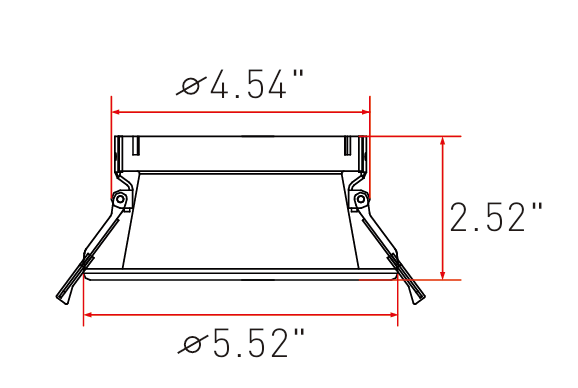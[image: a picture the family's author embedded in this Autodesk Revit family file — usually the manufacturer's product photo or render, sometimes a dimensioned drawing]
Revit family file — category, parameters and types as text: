
# Revit family: Alcon-14123-6R-WW-Revit-Family
name_source: partatom
category: Lighting Fixtures
units: mm (PartAtom-declared; Revit-internal decimal feet)

## family parameters
Always vertical = Yes
Cut with Voids When Loaded = No
Host = Ceiling
Light Source = Yes
OmniClass Number = 23.80.70.11
OmniClass Title = Luminaries for Internal Lighting
Part Type = Normal
Room Calculation Point = No
Round Connector Dimension = Use Diameter
Shared = No

## types (1)
- Type 1
    Color Filter = 16777215
    Default Elevation = 0' - 0"
    Dimming Lamp Color Temperature Shift = <None>
    Housing = <By Category>
    Light Source Symbol Length = 10' - 0"
    LightSource = <By Category>
    Link To Product Page = https://www.alconlighting.com
    Manufacturer = Alcon Light
    Product Identity = Alcon Lighting 14123-6R-WW
    Spot Beam Angle = 30.00°
    Spot Field Angle = 90.00°
    Tilt Angle = 60.00°

## geometry (parser evidence)
native form markers: Sweep x2
no freeform markers — native parametric forms only
